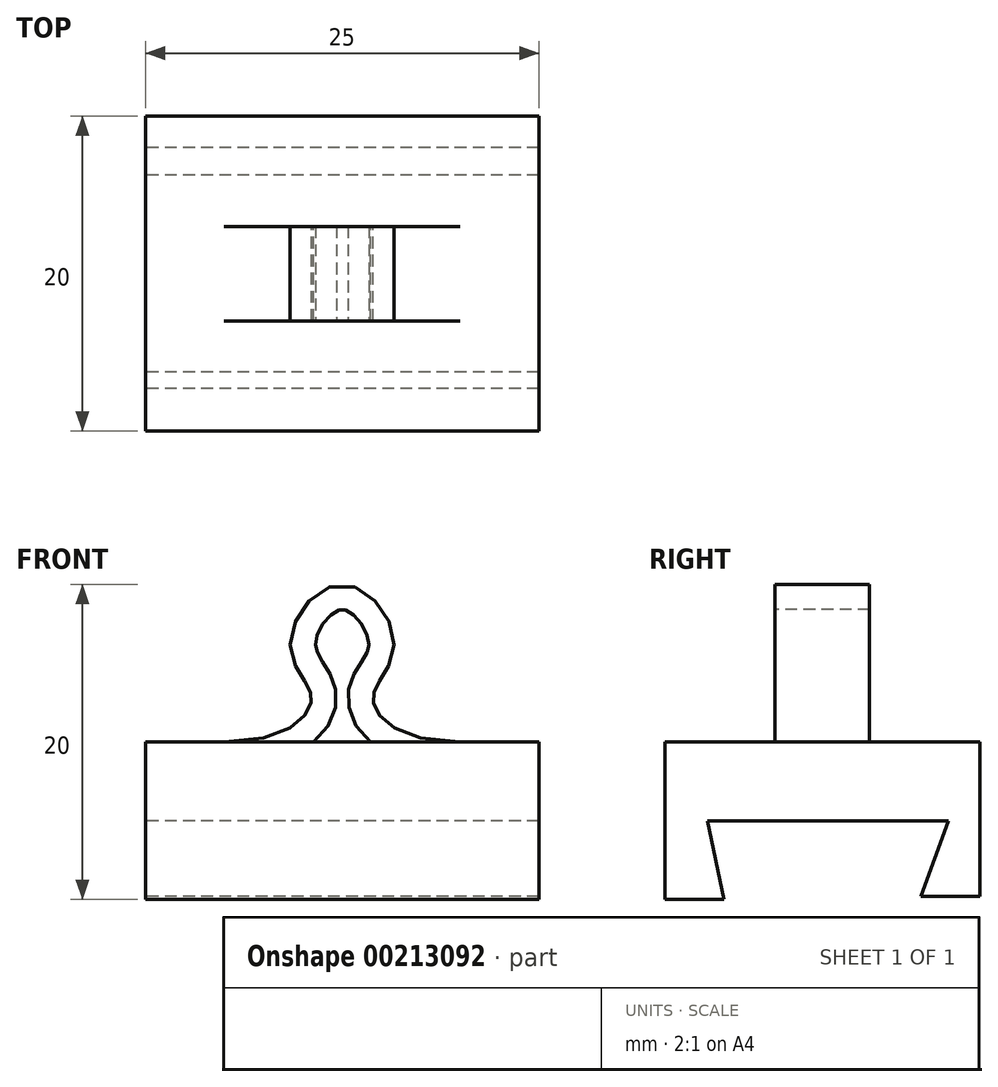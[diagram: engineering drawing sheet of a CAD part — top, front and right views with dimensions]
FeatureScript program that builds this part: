
annotation { "Feature Type Name" : "Feature", "Feature Type Description" : "" }
export const myFeature = defineFeature(function(context is Context, id is Id, definition is map)
    precondition{}
    {
        {
            var Q0;
            Q0=qCreatedBy(makeId("Front.planeOp"),FACE);
            var sketch = newSketch(context, id + "F0", { "sketchPlane" : qUnion([Q0])});
            skFitSpline(sketch, "E0", {"points": [v(0, 0) * mm, v(6.3, 4) * mm, v(5, 7) * mm, v(7.5, 10) * mm, v(10, 7) * mm, v(8.7, 4) * mm, v(15, 0) * mm], "startDerivative": vector(71.56, 0) * mm, "endDerivative": vector(71.56, 0) * mm});
            skLineSegment(sketch, "E1", {"start": v(0, 0) * mm, "end": v(-9.1, 0) * mm, "construction": true});
            skSolve(sketch);
        }
        {
            var Q0;
            Q0=sQuery(id+"F0.wireOp",EDGE,"E1");
            var Q1;
            Q1=sQuery(id+"F0.wireOp",VERTEX,"E0.start");
            cPlane(context, id + "F1", {"entities" : qUnion([Q0, Q1]), "cplaneType" : CPlaneType.LINE_POINT, "offset" : 25 * mm, "width" : 150 * mm, "height" : 150 * mm});
        }
        {
            var Q0;
            Q0=qCreatedBy(id+"F1.planeOp",FACE);
            var sketch = newSketch(context, id + "F2", { "sketchPlane" : qUnion([Q0])});
            skLineSegment(sketch, "E2.bottom", {"start": v(-3, 0.8) * mm, "end": v(3, 0.8) * mm});
            skLineSegment(sketch, "E2.top", {"start": v(-3, -0.8) * mm, "end": v(3, -0.8) * mm});
            skLineSegment(sketch, "E2.left", {"start": v(-3, 0.8) * mm, "end": v(-3, -0.8) * mm});
            skLineSegment(sketch, "E2.right", {"start": v(3, 0.8) * mm, "end": v(3, -0.8) * mm});
            skPoint(sketch, "E2.middle", {"position": v(0, 0) * mm});
            skSolve(sketch);
        }
        {
            var Q0;
            Q0 = qSketchRegion(id + "F2", true);
            var Q1;
            Q1 = qConstructionFilter(qBodyType(qCreatedBy(id + "F0" ,EDGE), BodyType.WIRE), ConstructionObject.NO);
            sweep(context, id + "F3", {"profiles" : qUnion([Q0]), "path" : qUnion([Q1])});
        }
        {
            var Q0;
            Q0=qCreatedBy(makeId("Right.planeOp"),FACE);
            var sketch = newSketch(context, id + "F4", { "sketchPlane" : qUnion([Q0])});
            skLineSegment(sketch, "E3", {"start": v(10, 0.8) * mm, "end": v(10, -9) * mm});
            skLineSegment(sketch, "E4", {"start": v(10, -9) * mm, "end": v(6.25, -9) * mm});
            skLineSegment(sketch, "E5", {"start": v(6.25, -9) * mm, "end": v(8, -4.2) * mm});
            skLineSegment(sketch, "E6", {"start": v(8, -4.2) * mm, "end": v(-7.3, -4.2) * mm});
            skLineSegment(sketch, "E7", {"start": v(-7.3, -4.2) * mm, "end": v(-6.25, -9.2) * mm});
            skLineSegment(sketch, "E8", {"start": v(-6.25, -9.2) * mm, "end": v(-10, -9.2) * mm});
            skLineSegment(sketch, "E9", {"start": v(-10, -9.2) * mm, "end": v(-10, 0.8) * mm});
            skLineSegment(sketch, "E10", {"start": v(-10, 0.8) * mm, "end": v(10, 0.8) * mm});
            skSolve(sketch);
        }
        {
            var Q0;
            Q0 = qSketchRegion(id + "F4", true);
            extrude(context, id + "F5", {"entities" : qUnion([Q0]), "operationType" : NewBodyOperationType.ADD, "depth" : 20 * mm, "hasSecondDirection" : true, "secondDirectionOppositeDirection" : true, "secondDirectionDepth" : 5 * mm});
        }
    });
